# Revit family: Electrical_Equipment-Floor_Box-Hubbell_Wiring-Single_Service_Metal_Concrete-B2537
name_source: partatom
category: Electrical Fixtures
revit_build: Autodesk Revit 2015 (Build: 20140606_1530(x64)
units: mm (PartAtom-declared; Revit-internal decimal feet)

## types (2) — shared parameters
Assembly Code = D5020115
Box Material = Metal-Hubbell-Cast Iron
Conduit Connector 1 Radius = 0' - 0 3/8"
Conduit Connector_1 Description = Conduit 0.75in. Connection
Conduit Connector_2 Description = Conduit 0.75in. Connection
Conduit Connector_3 Description = Conduit 0.75in. Connection
Conduit Connector_4 Description = Conduit 0.75in. Connection
Default Elevation = 0' - 0"
Description = Flush Round Single-Service Metal Concrete Floor Box
Manufacturer = Hubbell-Wiring
Product Documentation Link = http://ecatalog.hubbell-wiring.com
Product Page URL = http://ecatalog.hubbell-wiring.com
Product data url = https://bimobject.com
URL = http://www.hubbell-wiring.com

## per-type parameters (varying)
| type | Collar Material | Floor Box Type | Model |
| B2537 - Brass Collar - 0.75in Access | Metal-Hubbell-Brass | Metal Concrete Floor Box : B2537 - Metal Concrete Floor Box | B2537 |
| BA2537 - Aluminum Collar - 0.75in Access | Metal-Hubbell-Aluminum | Metal Concrete Floor Box : BA2537 - Metal Concrete Floor Box | BA2537 |

## geometry (parser evidence)
native form markers: Blend x24, Sweep x13
no freeform markers — native parametric forms only
